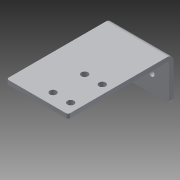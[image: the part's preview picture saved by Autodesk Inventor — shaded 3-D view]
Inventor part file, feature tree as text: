
AUTODESK INVENTOR PART (.ipt)
format: ipt  version: 2014 (Build 180170000, 170)  size: 130,048 bytes
history: native  units: in
note: dims shown in document units (in); Inventor stores cm internally (conversion verified against a paired STEP export)
features: sheet_metal_op x4, sketch x3, other x2, fillet x1, extrude x1
ambient origin geometry x8: Origin, YZ Plane, XZ Plane, XY Plane, X Axis, Y Axis, Z Axis, Center Point
bodies: Solid1 (feature_tree)
feature tree (11):
  sheet_metal_op  "Face1"
  sheet_metal_op  "Flange1"
  fillet  "Fillet1"  Radius=1.75in
  extrude  "Extrusion1"  Depth=0.163in
  sketch  "Sketch1"  dims[d1=1.0in d2=0.163in]
  other  "Plate1"
  sketch  "Sketch2"  dims[d4=0.7874in d6=1.0in d7=0.3937in d9=1.0in]
  other  "Plate2"
  sheet_metal_op  "Bend1"
  sheet_metal_op  "Corner1"
  sketch  "Sketch3"  dims[d11=0.125in d12=0.125in d13=0.0625in d14=0.25in d15=0.125in d16=3.0in d17=90.0deg d18=0.05in d19=0.5in d20=0.125in d21=0.125in d22=0.0625in d23=1.35in d24=0.75in d25=1.375in d27=0.19in d28=0.125in d29=0.2265in d30=1.0in d31=0.0in d34=0.25in d35=0.875in]
